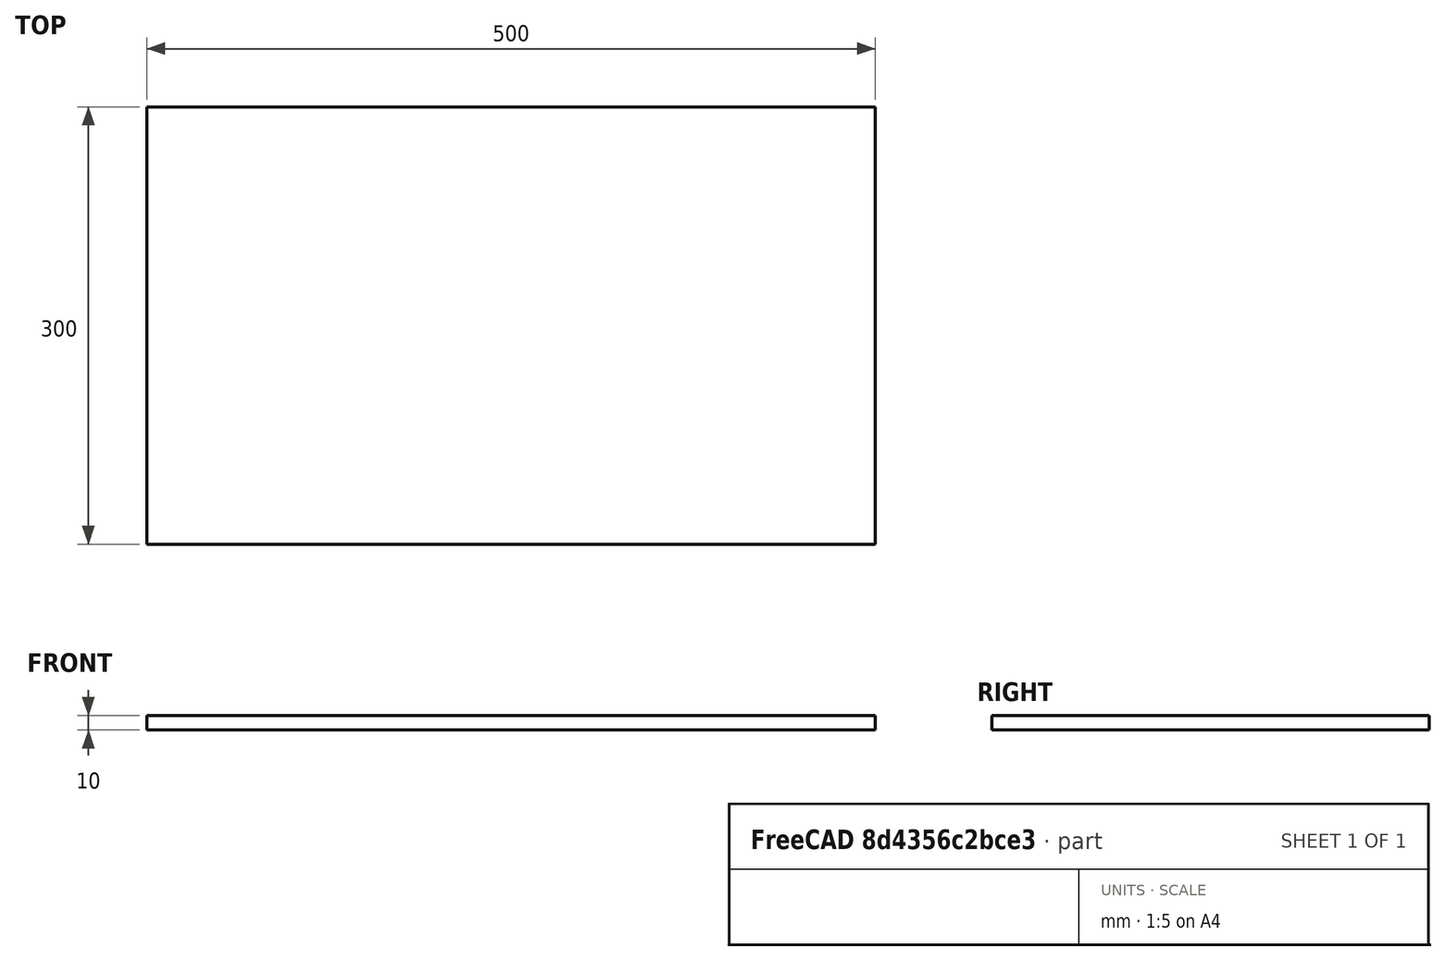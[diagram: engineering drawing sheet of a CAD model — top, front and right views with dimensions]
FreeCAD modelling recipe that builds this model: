
FCSTD DOCUMENT  (FreeCAD 1.0R39109 (Git))
Label: table_placeholder
License: All rights reserved
LicenseURL: http://en.wikipedia.org/wiki/All_rights_reserved
objects: Sketcher::SketchObject×1, PartDesign::Pad×1, PartDesign::Body×1
note: 6 computed .brp shape members not serialized (recipe doc carries the construction recipe); baked Part::Feature solids carry a one-line shape summary decoded from their .brp

FEATURE [Sketcher::SketchObject] Sketch
  ArcFitTolerance = 1e-06
  AttachmentSupport = -> [XY_Plane]
  FullyConstrained = true
  MakeInternals = false
  MapMode = 5
  sketch-geometry (5):
    g0: LineSegment StartX=250 StartY=-150 StartZ=0 EndX=250 EndY=150 EndZ=0
    g1: LineSegment StartX=250 StartY=150 StartZ=0 EndX=-250 EndY=150 EndZ=0
    g2: LineSegment StartX=-250 StartY=150 StartZ=0 EndX=-250 EndY=-150 EndZ=0
    g3: LineSegment StartX=-250 StartY=-150 StartZ=0 EndX=250 EndY=-150 EndZ=0
    g4: GeomPoint [constr] X=0 Y=0 Z=0
  constraints (12):
    c: Coincident(g0,g1)
    c: Coincident(g1,g2)
    c: Coincident(g2,g3)
    c: Coincident(g3,g0)
    c: Vertical(g0)
    c: Vertical(g2)
    c: Horizontal(g1)
    c: Horizontal(g3)
    c: Symmetric(g2,g0,g4)
    c: Coincident(g4,g-1)
    c: DistanceX(g3,g3) = 500
    c: DistanceY(g0,g0) = 300
FEATURE [PartDesign::Pad] Pad
  Direction = (0,0,1)
  Length = 10
  Length2 = 10
  Profile = -> Sketch
  ReferenceAxis = -> Sketch [N_Axis]
  Refine = true
  Suppressed = false
  Type = 0
FEATURE [PartDesign::Body] Body  label="table_body"
  AllowCompound = false
  Group = -> [Sketch,Pad]
  Origin = -> Origin
  Tip = -> Pad
